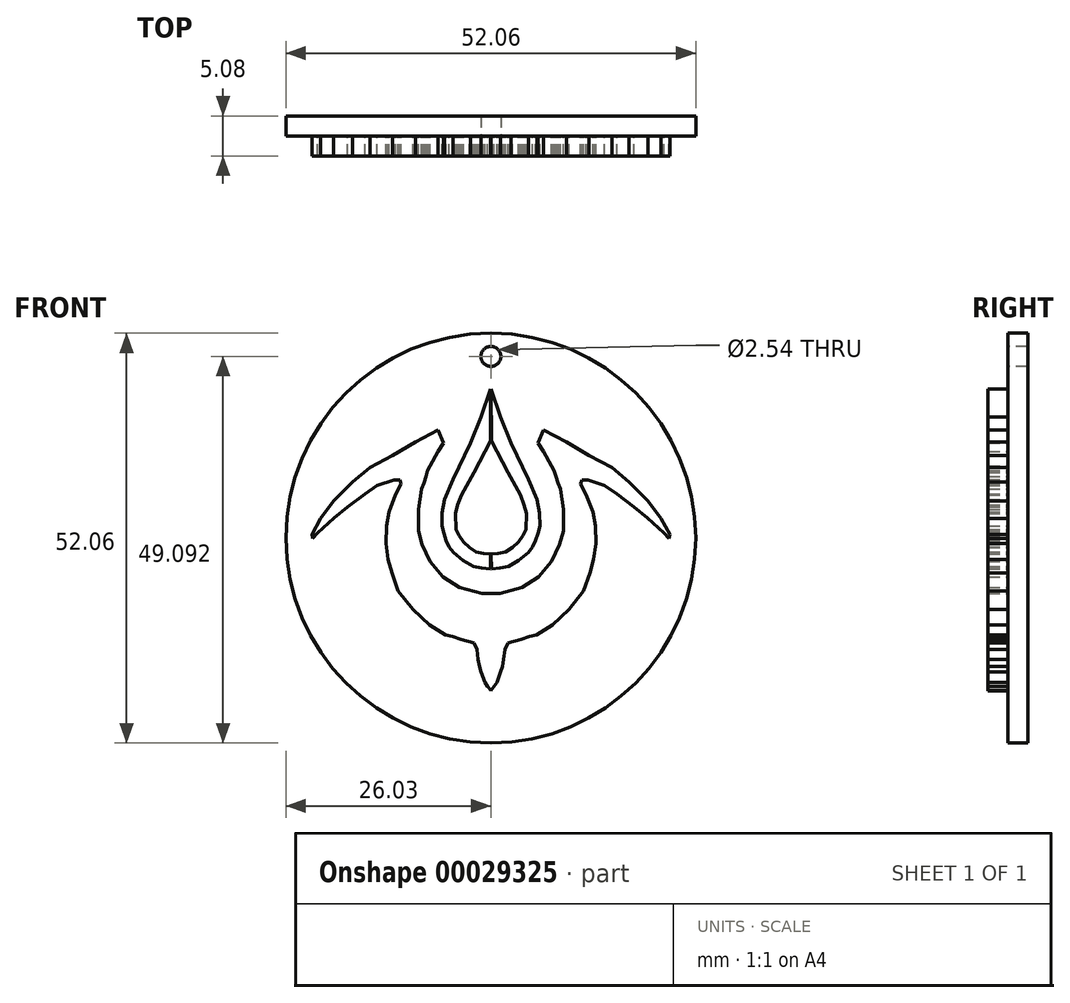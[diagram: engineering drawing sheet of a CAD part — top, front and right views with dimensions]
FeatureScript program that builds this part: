
annotation { "Feature Type Name" : "Feature", "Feature Type Description" : "" }
export const myFeature = defineFeature(function(context is Context, id is Id, definition is map)
    precondition{}
    {
        {
            var Q0;
            Q0=qCreatedBy(makeId("Front.planeOp"),FACE);
            var sketch = newSketch(context, id + "F0", { "sketchPlane" : qUnion([Q0])});
            skLineSegment(sketch, "E0", {"start": v(-11.37, 19.06) * mm, "end": v(-10.12, 15.4) * mm});
            skLineSegment(sketch, "E1", {"start": v(-10.12, 15.4) * mm, "end": v(-8.79, 12.07) * mm});
            skLineSegment(sketch, "E2", {"start": v(-8.79, 12.07) * mm, "end": v(-6.56, 7.42) * mm});
            skLineSegment(sketch, "E3", {"start": v(-6.56, 7.42) * mm, "end": v(-5.47, 4.88) * mm});
            skLineSegment(sketch, "E4", {"start": v(-5.47, 4.88) * mm, "end": v(-5.15, 3.2) * mm});
            skLineSegment(sketch, "E5", {"start": v(-5.15, 3.2) * mm, "end": v(-5.12, 1.52) * mm});
            skLineSegment(sketch, "E6", {"start": v(-5.12, 1.52) * mm, "end": v(-5.4, 0.6) * mm});
            skLineSegment(sketch, "E7", {"start": v(-5.4, 0.6) * mm, "end": v(-5.68, -0.3) * mm});
            skLineSegment(sketch, "E8", {"start": v(-5.68, -0.3) * mm, "end": v(-6.06, -1.14) * mm});
            skLineSegment(sketch, "E9", {"start": v(-6.06, -1.14) * mm, "end": v(-6.6, -1.84) * mm});
            skLineSegment(sketch, "E10", {"start": v(-6.6, -1.84) * mm, "end": v(-7.83, -2.87) * mm});
            skLineSegment(sketch, "E11", {"start": v(-7.83, -2.87) * mm, "end": v(-9.14, -3.6) * mm});
            skLineSegment(sketch, "E12", {"start": v(-9.14, -3.6) * mm, "end": v(-10.18, -3.8) * mm});
            skLineSegment(sketch, "E13", {"start": v(-10.18, -3.8) * mm, "end": v(-11.29, -3.94) * mm});
            skLineSegment(sketch, "E14", {"start": v(-11.29, -3.94) * mm, "end": v(-11.33, -2.03) * mm});
            skLineSegment(sketch, "E15", {"start": v(-11.33, -2.03) * mm, "end": v(-10.45, -1.99) * mm});
            skLineSegment(sketch, "E16", {"start": v(-10.45, -1.99) * mm, "end": v(-9.5, -1.8) * mm});
            skLineSegment(sketch, "E17", {"start": v(-9.5, -1.8) * mm, "end": v(-8.64, -1.22) * mm});
            skLineSegment(sketch, "E18", {"start": v(-8.64, -1.22) * mm, "end": v(-7.85, -0.5) * mm});
            skLineSegment(sketch, "E19", {"start": v(-7.85, -0.5) * mm, "end": v(-7.28, 0.35) * mm});
            skLineSegment(sketch, "E20", {"start": v(-7.28, 0.35) * mm, "end": v(-6.92, 1.06) * mm});
            skLineSegment(sketch, "E21", {"start": v(-6.92, 1.06) * mm, "end": v(-6.84, 3.09) * mm});
            skLineSegment(sketch, "E22", {"start": v(-6.84, 3.09) * mm, "end": v(-7.13, 4.2) * mm});
            skLineSegment(sketch, "E23", {"start": v(-7.13, 4.2) * mm, "end": v(-7.62, 5.47) * mm});
            skLineSegment(sketch, "E24", {"start": v(-7.62, 5.47) * mm, "end": v(-9.18, 8.32) * mm});
            skLineSegment(sketch, "E25", {"start": v(-9.18, 8.32) * mm, "end": v(-11.29, 12.3) * mm});
            skLineSegment(sketch, "E26", {"start": v(-11.29, 12.3) * mm, "end": v(-11.33, 19.41) * mm});
            skLineSegment(sketch, "E27", {"start": v(-11.33, 19.41) * mm, "end": v(-11.37, 19.06) * mm});
            skLineSegment(sketch, "E28", {"start": v(-11.37, -19.41) * mm, "end": v(-10.93, -18.84) * mm});
            skLineSegment(sketch, "E29", {"start": v(-10.93, -18.84) * mm, "end": v(-10.59, -18.32) * mm});
            skLineSegment(sketch, "E30", {"start": v(-10.59, -18.32) * mm, "end": v(-10.12, -17) * mm});
            skLineSegment(sketch, "E31", {"start": v(-10.12, -17) * mm, "end": v(-9.9, -16.3) * mm});
            skLineSegment(sketch, "E32", {"start": v(-9.9, -16.3) * mm, "end": v(-9.73, -15.43) * mm});
            skLineSegment(sketch, "E33", {"start": v(-9.73, -15.43) * mm, "end": v(-9.57, -14.18) * mm});
            skLineSegment(sketch, "E34", {"start": v(-9.57, -14.18) * mm, "end": v(-9.2, -13.34) * mm});
            skLineSegment(sketch, "E35", {"start": v(-9.2, -13.34) * mm, "end": v(-7.54, -12.87) * mm});
            skLineSegment(sketch, "E36", {"start": v(-7.54, -12.87) * mm, "end": v(-6.46, -12.54) * mm});
            skLineSegment(sketch, "E37", {"start": v(-6.46, -12.54) * mm, "end": v(-5.59, -12.3) * mm});
            skLineSegment(sketch, "E38", {"start": v(-5.59, -12.3) * mm, "end": v(-3.56, -11.05) * mm});
            skLineSegment(sketch, "E39", {"start": v(-3.56, -11.05) * mm, "end": v(-1.45, -9.1) * mm});
            skLineSegment(sketch, "E40", {"start": v(-1.45, -9.1) * mm, "end": v(0.43, -6.76) * mm});
            skLineSegment(sketch, "E41", {"start": v(0.43, -6.76) * mm, "end": v(1.2, -4.41) * mm});
            skLineSegment(sketch, "E42", {"start": v(1.2, -4.41) * mm, "end": v(1.68, -2.7) * mm});
            skLineSegment(sketch, "E43", {"start": v(1.68, -2.7) * mm, "end": v(2, -0.66) * mm});
            skLineSegment(sketch, "E44", {"start": v(2, -0.66) * mm, "end": v(1.91, 1.52) * mm});
            skLineSegment(sketch, "E45", {"start": v(1.91, 1.52) * mm, "end": v(1.6, 3.32) * mm});
            skLineSegment(sketch, "E46", {"start": v(1.6, 3.32) * mm, "end": v(0.74, 5.5) * mm});
            skLineSegment(sketch, "E47", {"start": v(0.74, 5.5) * mm, "end": v(0.04, 6.84) * mm});
            skLineSegment(sketch, "E48", {"start": v(0.04, 6.84) * mm, "end": v(0.2, 7.38) * mm});
            skLineSegment(sketch, "E49", {"start": v(0.2, 7.38) * mm, "end": v(0.98, 7.38) * mm});
            skLineSegment(sketch, "E50", {"start": v(0.98, 7.38) * mm, "end": v(3.09, 6.68) * mm});
            skLineSegment(sketch, "E51", {"start": v(3.09, 6.68) * mm, "end": v(4.65, 5.59) * mm});
            skLineSegment(sketch, "E52", {"start": v(4.65, 5.59) * mm, "end": v(6.84, 3.95) * mm});
            skLineSegment(sketch, "E53", {"start": v(6.84, 3.95) * mm, "end": v(8.55, 2.54) * mm});
            skLineSegment(sketch, "E54", {"start": v(8.55, 2.54) * mm, "end": v(10.66, 0.66) * mm});
            skLineSegment(sketch, "E55", {"start": v(10.66, 0.66) * mm, "end": v(11.29, -0.04) * mm});
            skLineSegment(sketch, "E56", {"start": v(11.29, -0.04) * mm, "end": v(11.37, 0.43) * mm});
            skLineSegment(sketch, "E57", {"start": v(11.37, 0.43) * mm, "end": v(10.27, 2.46) * mm});
            skLineSegment(sketch, "E58", {"start": v(10.27, 2.46) * mm, "end": v(8.63, 4.73) * mm});
            skLineSegment(sketch, "E59", {"start": v(8.63, 4.73) * mm, "end": v(6.21, 7.15) * mm});
            skLineSegment(sketch, "E60", {"start": v(6.21, 7.15) * mm, "end": v(4.02, 8.95) * mm});
            skLineSegment(sketch, "E61", {"start": v(4.02, 8.95) * mm, "end": v(1.13, 10.5) * mm});
            skLineSegment(sketch, "E62", {"start": v(1.13, 10.5) * mm, "end": v(-1.76, 12.23) * mm});
            skLineSegment(sketch, "E63", {"start": v(-1.76, 12.23) * mm, "end": v(-4.65, 13.71) * mm});
            skLineSegment(sketch, "E64", {"start": v(-4.65, 13.71) * mm, "end": v(-5.35, 12.07) * mm});
            skLineSegment(sketch, "E65", {"start": v(-5.35, 12.07) * mm, "end": v(-4.65, 10.98) * mm});
            skLineSegment(sketch, "E66", {"start": v(-4.65, 10.98) * mm, "end": v(-3.63, 9.18) * mm});
            skLineSegment(sketch, "E67", {"start": v(-3.63, 9.18) * mm, "end": v(-3.34, 8.6) * mm});
            skLineSegment(sketch, "E68", {"start": v(-3.34, 8.6) * mm, "end": v(-3.09, 7.84) * mm});
            skLineSegment(sketch, "E69", {"start": v(-3.09, 7.84) * mm, "end": v(-2.84, 7) * mm});
            skLineSegment(sketch, "E70", {"start": v(-2.84, 7) * mm, "end": v(-2.54, 6.21) * mm});
            skLineSegment(sketch, "E71", {"start": v(-2.54, 6.21) * mm, "end": v(-2.15, 3.63) * mm});
            skLineSegment(sketch, "E72", {"start": v(-2.15, 3.63) * mm, "end": v(-2.15, 0.9) * mm});
            skLineSegment(sketch, "E73", {"start": v(-2.15, 0.9) * mm, "end": v(-2.62, -0.82) * mm});
            skLineSegment(sketch, "E74", {"start": v(-2.62, -0.82) * mm, "end": v(-3.63, -3) * mm});
            skLineSegment(sketch, "E75", {"start": v(-3.63, -3) * mm, "end": v(-5.27, -4.96) * mm});
            skLineSegment(sketch, "E76", {"start": v(-5.27, -4.96) * mm, "end": v(-7.38, -6.29) * mm});
            skLineSegment(sketch, "E77", {"start": v(-7.38, -6.29) * mm, "end": v(-10.2, -7.07) * mm});
            skLineSegment(sketch, "E78", {"start": v(-10.2, -7.07) * mm, "end": v(-11.37, -7.07) * mm});
            skLineSegment(sketch, "E79", {"start": v(-11.37, -7.07) * mm, "end": v(-11.37, -19.41) * mm});
            skSolve(sketch);
        }
        {
            var Q0;
            {var subQ4=sQuery(id+"F0.wireOp",EDGE,"E1");Q0=makeQuery(id+"F0.imprint","IMPRINT",FACE,{"disambiguationData":[TD([[makeQuery(id+"F0.imprint","IMPRINT",EDGE,{"derivedFrom":subQ4}),-1.0]])]});}
            var Q1;
            Q1=makeQuery(id+"F0.imprint","IMPRINT",FACE,{"disambiguationData":[TD([[makeQuery(id+"F0.imprint","IMPRINT",EDGE,{"derivedFrom":sQuery(id+"F0.wireOp",EDGE,"E28")}),1.0]])]});
            extrude(context, id + "F1", {"entities" : qUnion([Q0, Q1]), "depth" : 2.54 * mm});
        }
        {
            var Q0;
            Q0=makeQuery(id+"F1.opExtrude","SWEPT_BODY",BODY,{"disambiguationData":[OSD([sQuery(id+"F0.wireOp",EDGE,"E28"),sQuery(id+"F0.wireOp",EDGE,"E29"),sQuery(id+"F0.wireOp",EDGE,"E30"),sQuery(id+"F0.wireOp",EDGE,"E31"),sQuery(id+"F0.wireOp",EDGE,"E32"),sQuery(id+"F0.wireOp",EDGE,"E33"),sQuery(id+"F0.wireOp",EDGE,"E34"),sQuery(id+"F0.wireOp",EDGE,"E35"),sQuery(id+"F0.wireOp",EDGE,"E36"),sQuery(id+"F0.wireOp",EDGE,"E37"),sQuery(id+"F0.wireOp",EDGE,"E38"),sQuery(id+"F0.wireOp",EDGE,"E39"),sQuery(id+"F0.wireOp",EDGE,"E40"),sQuery(id+"F0.wireOp",EDGE,"E41"),sQuery(id+"F0.wireOp",EDGE,"E42"),sQuery(id+"F0.wireOp",EDGE,"E43"),sQuery(id+"F0.wireOp",EDGE,"E44"),sQuery(id+"F0.wireOp",EDGE,"E45"),sQuery(id+"F0.wireOp",EDGE,"E46"),sQuery(id+"F0.wireOp",EDGE,"E47"),sQuery(id+"F0.wireOp",EDGE,"E48"),sQuery(id+"F0.wireOp",EDGE,"E49"),sQuery(id+"F0.wireOp",EDGE,"E50"),sQuery(id+"F0.wireOp",EDGE,"E51"),sQuery(id+"F0.wireOp",EDGE,"E52"),sQuery(id+"F0.wireOp",EDGE,"E53"),sQuery(id+"F0.wireOp",EDGE,"E54"),sQuery(id+"F0.wireOp",EDGE,"E55"),sQuery(id+"F0.wireOp",EDGE,"E56"),sQuery(id+"F0.wireOp",EDGE,"E57"),sQuery(id+"F0.wireOp",EDGE,"E58"),sQuery(id+"F0.wireOp",EDGE,"E59"),sQuery(id+"F0.wireOp",EDGE,"E60"),sQuery(id+"F0.wireOp",EDGE,"E61"),sQuery(id+"F0.wireOp",EDGE,"E62"),sQuery(id+"F0.wireOp",EDGE,"E63"),sQuery(id+"F0.wireOp",EDGE,"E64"),sQuery(id+"F0.wireOp",EDGE,"E65"),sQuery(id+"F0.wireOp",EDGE,"E66"),sQuery(id+"F0.wireOp",EDGE,"E67"),sQuery(id+"F0.wireOp",EDGE,"E68"),sQuery(id+"F0.wireOp",EDGE,"E69"),sQuery(id+"F0.wireOp",EDGE,"E70"),sQuery(id+"F0.wireOp",EDGE,"E71"),sQuery(id+"F0.wireOp",EDGE,"E72"),sQuery(id+"F0.wireOp",EDGE,"E73"),sQuery(id+"F0.wireOp",EDGE,"E74"),sQuery(id+"F0.wireOp",EDGE,"E75"),sQuery(id+"F0.wireOp",EDGE,"E76"),sQuery(id+"F0.wireOp",EDGE,"E77"),sQuery(id+"F0.wireOp",EDGE,"E78"),sQuery(id+"F0.wireOp",EDGE,"E79")])]});
            var Q1;
            Q1=makeQuery(id+"F1.opExtrude","SWEPT_BODY",BODY,{"disambiguationData":[OSD([sQuery(id+"F0.wireOp",EDGE,"E0"),sQuery(id+"F0.wireOp",EDGE,"E1"),sQuery(id+"F0.wireOp",EDGE,"E2"),sQuery(id+"F0.wireOp",EDGE,"E3"),sQuery(id+"F0.wireOp",EDGE,"E4"),sQuery(id+"F0.wireOp",EDGE,"E5"),sQuery(id+"F0.wireOp",EDGE,"E6"),sQuery(id+"F0.wireOp",EDGE,"E7"),sQuery(id+"F0.wireOp",EDGE,"E8"),sQuery(id+"F0.wireOp",EDGE,"E9"),sQuery(id+"F0.wireOp",EDGE,"E10"),sQuery(id+"F0.wireOp",EDGE,"E11"),sQuery(id+"F0.wireOp",EDGE,"E12"),sQuery(id+"F0.wireOp",EDGE,"E13"),sQuery(id+"F0.wireOp",EDGE,"E14"),sQuery(id+"F0.wireOp",EDGE,"E15"),sQuery(id+"F0.wireOp",EDGE,"E16"),sQuery(id+"F0.wireOp",EDGE,"E17"),sQuery(id+"F0.wireOp",EDGE,"E18"),sQuery(id+"F0.wireOp",EDGE,"E19"),sQuery(id+"F0.wireOp",EDGE,"E20"),sQuery(id+"F0.wireOp",EDGE,"E21"),sQuery(id+"F0.wireOp",EDGE,"E22"),sQuery(id+"F0.wireOp",EDGE,"E23"),sQuery(id+"F0.wireOp",EDGE,"E24"),sQuery(id+"F0.wireOp",EDGE,"E25"),sQuery(id+"F0.wireOp",EDGE,"E26")])]});
            transform(context, id + "F2", {"entities" : qUnion([Q0, Q1]), "transformType" : TransformType.TRANSLATION_3D, "dx" : 11.35 * mm, "dy" : 0 * mm, "dz" : 0 * mm, "makeCopy" : false});
        }
        {
            var Q0;
            Q0=makeQuery(id+"F1.opExtrude","SWEPT_BODY",BODY,{"disambiguationData":[OSD([sQuery(id+"F0.wireOp",EDGE,"E28"),sQuery(id+"F0.wireOp",EDGE,"E29"),sQuery(id+"F0.wireOp",EDGE,"E30"),sQuery(id+"F0.wireOp",EDGE,"E31"),sQuery(id+"F0.wireOp",EDGE,"E32"),sQuery(id+"F0.wireOp",EDGE,"E33"),sQuery(id+"F0.wireOp",EDGE,"E34"),sQuery(id+"F0.wireOp",EDGE,"E35"),sQuery(id+"F0.wireOp",EDGE,"E36"),sQuery(id+"F0.wireOp",EDGE,"E37"),sQuery(id+"F0.wireOp",EDGE,"E38"),sQuery(id+"F0.wireOp",EDGE,"E39"),sQuery(id+"F0.wireOp",EDGE,"E40"),sQuery(id+"F0.wireOp",EDGE,"E41"),sQuery(id+"F0.wireOp",EDGE,"E42"),sQuery(id+"F0.wireOp",EDGE,"E43"),sQuery(id+"F0.wireOp",EDGE,"E44"),sQuery(id+"F0.wireOp",EDGE,"E45"),sQuery(id+"F0.wireOp",EDGE,"E46"),sQuery(id+"F0.wireOp",EDGE,"E47"),sQuery(id+"F0.wireOp",EDGE,"E48"),sQuery(id+"F0.wireOp",EDGE,"E49"),sQuery(id+"F0.wireOp",EDGE,"E50"),sQuery(id+"F0.wireOp",EDGE,"E51"),sQuery(id+"F0.wireOp",EDGE,"E52"),sQuery(id+"F0.wireOp",EDGE,"E53"),sQuery(id+"F0.wireOp",EDGE,"E54"),sQuery(id+"F0.wireOp",EDGE,"E55"),sQuery(id+"F0.wireOp",EDGE,"E56"),sQuery(id+"F0.wireOp",EDGE,"E57"),sQuery(id+"F0.wireOp",EDGE,"E58"),sQuery(id+"F0.wireOp",EDGE,"E59"),sQuery(id+"F0.wireOp",EDGE,"E60"),sQuery(id+"F0.wireOp",EDGE,"E61"),sQuery(id+"F0.wireOp",EDGE,"E62"),sQuery(id+"F0.wireOp",EDGE,"E63"),sQuery(id+"F0.wireOp",EDGE,"E64"),sQuery(id+"F0.wireOp",EDGE,"E65"),sQuery(id+"F0.wireOp",EDGE,"E66"),sQuery(id+"F0.wireOp",EDGE,"E67"),sQuery(id+"F0.wireOp",EDGE,"E68"),sQuery(id+"F0.wireOp",EDGE,"E69"),sQuery(id+"F0.wireOp",EDGE,"E70"),sQuery(id+"F0.wireOp",EDGE,"E71"),sQuery(id+"F0.wireOp",EDGE,"E72"),sQuery(id+"F0.wireOp",EDGE,"E73"),sQuery(id+"F0.wireOp",EDGE,"E74"),sQuery(id+"F0.wireOp",EDGE,"E75"),sQuery(id+"F0.wireOp",EDGE,"E76"),sQuery(id+"F0.wireOp",EDGE,"E77"),sQuery(id+"F0.wireOp",EDGE,"E78"),sQuery(id+"F0.wireOp",EDGE,"E79")])]});
            var Q1;
            Q1=makeQuery(id+"F1.opExtrude","SWEPT_BODY",BODY,{"disambiguationData":[OSD([sQuery(id+"F0.wireOp",EDGE,"E0"),sQuery(id+"F0.wireOp",EDGE,"E1"),sQuery(id+"F0.wireOp",EDGE,"E2"),sQuery(id+"F0.wireOp",EDGE,"E3"),sQuery(id+"F0.wireOp",EDGE,"E4"),sQuery(id+"F0.wireOp",EDGE,"E5"),sQuery(id+"F0.wireOp",EDGE,"E6"),sQuery(id+"F0.wireOp",EDGE,"E7"),sQuery(id+"F0.wireOp",EDGE,"E8"),sQuery(id+"F0.wireOp",EDGE,"E9"),sQuery(id+"F0.wireOp",EDGE,"E10"),sQuery(id+"F0.wireOp",EDGE,"E11"),sQuery(id+"F0.wireOp",EDGE,"E12"),sQuery(id+"F0.wireOp",EDGE,"E13"),sQuery(id+"F0.wireOp",EDGE,"E14"),sQuery(id+"F0.wireOp",EDGE,"E15"),sQuery(id+"F0.wireOp",EDGE,"E16"),sQuery(id+"F0.wireOp",EDGE,"E17"),sQuery(id+"F0.wireOp",EDGE,"E18"),sQuery(id+"F0.wireOp",EDGE,"E19"),sQuery(id+"F0.wireOp",EDGE,"E20"),sQuery(id+"F0.wireOp",EDGE,"E21"),sQuery(id+"F0.wireOp",EDGE,"E22"),sQuery(id+"F0.wireOp",EDGE,"E23"),sQuery(id+"F0.wireOp",EDGE,"E24"),sQuery(id+"F0.wireOp",EDGE,"E25"),sQuery(id+"F0.wireOp",EDGE,"E26")])]});
            var Q2;
            Q2=qCreatedBy(makeId("Right.planeOp"),FACE);
            mirror(context, id + "F3", {"operationType" : NewBodyOperationType.ADD, "entities" : qUnion([Q0, Q1]), "mirrorPlane" : qUnion([Q2])});
        }
        {
            var Q0;
            Q0=qCreatedBy(makeId("Front.planeOp"),FACE);
            var sketch = newSketch(context, id + "F4", { "sketchPlane" : qUnion([Q0])});
            skCircle(sketch, "E80", {"center": v(0, 0) * mm, "radius": 26.03 * mm});
            skSolve(sketch);
        }
        {
            var Q0;
            Q0=makeQuery(id+"F4.imprint","IMPRINT",FACE,{"disambiguationData":[TD([[makeQuery(id+"F4.imprint","IMPRINT",EDGE,{"derivedFrom":sQuery(id+"F4.wireOp",EDGE,"E80")}),1.0]])]});
            extrude(context, id + "F5", {"entities" : qUnion([Q0]), "oppositeDirection" : true, "depth" : 2.54 * mm});
        }
        {
            var Q0;
            Q0=makeQuery(id+"F5.opExtrude","CAP_FACE",FACE,{"disambiguationData":[OSD([sQuery(id+"F4.wireOp",EDGE,"E80")])],"isStart":true});
            var sketch = newSketch(context, id + "F6", { "sketchPlane" : qUnion([Q0])});
            skPoint(sketch, "E81", {"position": v(0, 23.06) * mm});
            skCircle(sketch, "E82", {"center": v(0, 23.06) * mm, "radius": 1.58 * mm});
            skSolve(sketch);
        }
        {
            var Q0;
            Q0=sQuery(id+"F6.wireOp",VERTEX,"E81");
            var Q1;
            Q1=makeQuery(id+"F5.opExtrude","SWEPT_BODY",BODY,{"disambiguationData":[OSD([sQuery(id+"F4.wireOp",EDGE,"E80")])]});
            hole(context, id + "F7", {"style" : HoleStyle.SIMPLE, "holeDiameter" : 2.54 * mm, "endStyle" : HoleEndStyle.THROUGH, "locations" : qUnion([Q0]), "scope" : qUnion([Q1])});
        }
    });
